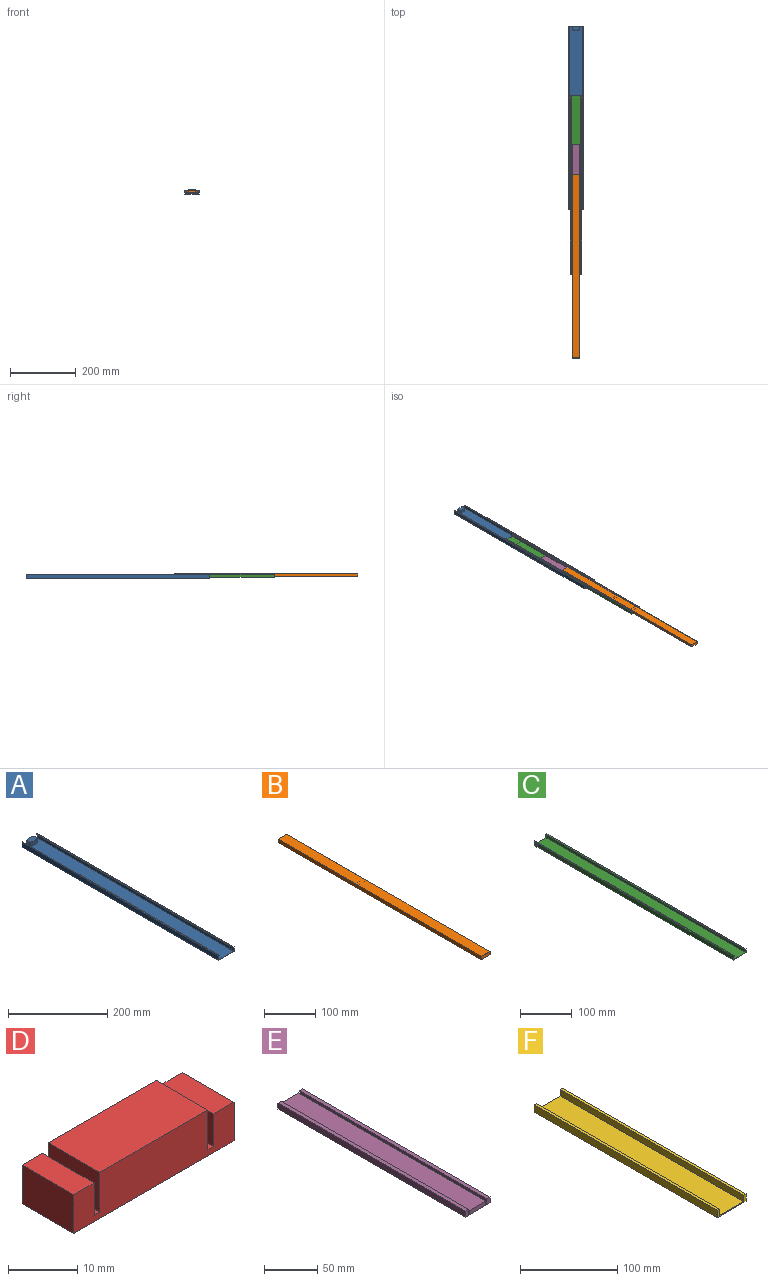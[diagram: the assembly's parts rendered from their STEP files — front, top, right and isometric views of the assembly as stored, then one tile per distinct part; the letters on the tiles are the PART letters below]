
ASSEMBLY  parts=6 mates=4
PART A: 30 faces, bbox 44.5x558.8x11.6 mm
  f0: plane 549.91x1.4mm, normal (0,0,-1), area 768.2mm2, adj f7,f8,f16,f28
  f1: plane 9.14x4.57mm, normal (-1,0,0), area 41.8mm2, adj f2,f5,f14,f29
  f2: plane 558.8x42.16mm, normal (0,0,1), area 23290.7mm2, adj f1,f4,f5,f6,f7,f8,f16,f17
  f3: plane 4.57x1.4mm, normal (0,0,-1), area 6.4mm2, adj f5,f6,f17,f27
  f4: plane 549.91x9.14mm, normal (1,0,0), area 5028.4mm2, adj f2,f7,f15,f26
  f5: plane 44.45x11.43mm, normal (0,-1,0), area 77.5mm2, adj f1,f2,f3,f6,f8,f9,f10,f11
  f6: plane 558.8x10.29mm, normal (1,0,0), area 678.2mm2, adj f2,f3,f5,f7,f10,f15,f26,f27
  f7: plane 44.45x11.56mm, normal (0,1,0), area 201.8mm2, adj f0,f2,f4,f6,f8,f9,f10,f11
  f8: plane 558.8x10.29mm, normal (-1,0,0), area 678.2mm2, adj f0,f2,f5,f7,f9,f14,f28,f29
  f9: plane 558.8x2.54mm, normal (0,0,1), area 1419.4mm2, adj f5,f7,f8,f11
  f10: plane 558.8x2.54mm, normal (0,0,1), area 1419.4mm2, adj f5,f6,f7,f12
  f11: plane 558.8x11.43mm, normal (1,0,0), area 6387.1mm2, adj f5,f7,f9,f13
  f12: plane 558.8x11.43mm, normal (-1,0,0), area 6387.1mm2, adj f5,f7,f10,f13
  f13: plane 558.8x44.45mm, normal (0,0,-1), area 24838.7mm2, adj f5,f7,f11,f12
  f14: plane 4.57x1.4mm, normal (0,0,-1), area 6.4mm2, adj f1,f5,f8,f29
  f15: plane 549.91x1.4mm, normal (0,0,-1), area 768.2mm2, adj f4,f6,f7,f26
  f16: plane 549.91x9.14mm, normal (-1,0,0), area 5028.4mm2, adj f0,f2,f7,f28
  f17: plane 9.14x4.57mm, normal (1,0,0), area 41.8mm2, adj f2,f3,f5,f27
  f18: plane 22.1x12.7mm, normal (0,0,1), area 258.5mm2, adj f7,f19,f20,f21,f22,f23,f24,f25
  f19: plane 10.41x2.54mm, normal (-1,0,0), area 26.5mm2, adj f2,f18,f23,f24
  f20: plane 10.41x2.54mm, normal (1,0,0), area 26.5mm2, adj f2,f18,f22,f25
  f21: plane 11.94x10.41mm, normal (0,-1,0), area 124.3mm2, adj f2,f18,f24,f25
  f22: cylinder r=5.08mm len=10.41mm, axis (0,0,-1), area 83.1mm2, adj f2,f7,f18,f20
  f23: cylinder r=5.08mm len=10.41mm, axis (0,0,1), area 83.1mm2, adj f2,f7,f18,f19
  f24: cylinder r=5.08mm len=10.41mm, axis (0,0,1), area 83.1mm2, adj f2,f18,f19,f21
  f25: cylinder r=5.08mm len=10.41mm, axis (0,0,-1), area 83.1mm2, adj f2,f18,f20,f21
  f26: plane 9.14x1.4mm, normal (0,1,0), area 12.8mm2, adj f2,f4,f6,f15
  f27: plane 9.14x1.4mm, normal (0,-1,0), area 12.8mm2, adj f2,f3,f6,f17
  f28: plane 9.14x1.4mm, normal (0,1,0), area 12.8mm2, adj f0,f2,f8,f16
  f29: plane 9.14x1.4mm, normal (0,-1,0), area 12.8mm2, adj f1,f2,f8,f14
PART B: 14 faces, bbox 24.4x558.8x8.1 mm
  f0: plane 212.73x22.1mm, normal (0,0,-1), area 4700.8mm2, adj f1,f2,f6,f12
  f1: plane 557.66x6.99mm, normal (1,0,0), area 3884.8mm2, adj f0,f3,f5,f6,f10,f11,f12,f13
  f2: plane 557.66x6.99mm, normal (-1,0,0), area 3884.8mm2, adj f0,f3,f5,f6,f10,f11,f12,f13
  f3: plane 338.58x22.1mm, normal (0,0,-1), area 7482mm2, adj f1,f2,f10,f11
  f4: plane 24.38x8.13mm, normal (0,-1,0), area 198.2mm2, adj f5,f7,f8,f9
  f5: plane 558.8x24.38mm, normal (0,0,-1), area 1302.7mm2, adj f1,f2,f4,f6,f7,f9,f10
  f6: plane 24.38x8.13mm, normal (0,1,0), area 43.8mm2, adj f0,f1,f2,f5,f7,f8,f9
  f7: plane 558.8x8.13mm, normal (1,0,0), area 4541.9mm2, adj f4,f5,f6,f8
  f8: plane 558.8x24.38mm, normal (0,0,1), area 13625.8mm2, adj f4,f6,f7,f9
  f9: plane 558.8x8.13mm, normal (-1,0,0), area 4541.9mm2, adj f4,f5,f6,f8
  f10: plane 22.1x6.99mm, normal (0,1,0), area 154.4mm2, adj f1,f2,f3,f5
  f11: plane 22.1x1.65mm, normal (0,-1,0), area 36.5mm2, adj f1,f2,f3,f13
  f12: plane 22.1x1.65mm, normal (0,1,0), area 36.5mm2, adj f0,f1,f2,f13
  f13: plane 22.1x6.35mm, normal (0,0,-1), area 140.3mm2, adj f1,f2,f11,f12
PART C: 24 faces, bbox 37.3x546.1x9.1 mm
  f0: plane 9.14x4.57mm, normal (-1,0,0), area 41.8mm2, adj f12,f14,f15,f21
  f1: plane 537.21x9.14mm, normal (1,0,0), area 4912.2mm2, adj f9,f10,f12,f19
  f2: plane 544.96x6.86mm, normal (1,0,0), area 3737.3mm2, adj f6,f7,f9,f17
  f3: plane 544.96x1.4mm, normal (0,0,-1), area 761.3mm2, adj f4,f5,f9,f16
  f4: plane 546.1x8mm, normal (-1,0,0), area 632mm2, adj f3,f6,f9,f10,f15,f16
  f5: plane 544.96x6.86mm, normal (-1,0,0), area 3737.3mm2, adj f3,f6,f9,f16
  f6: plane 546.1x32.77mm, normal (0,0,1), area 17890.3mm2, adj f2,f4,f5,f8,f9,f15,f16,f17
  f7: plane 544.96x1.4mm, normal (0,0,-1), area 761.3mm2, adj f2,f8,f9,f17
  f8: plane 546.1x8mm, normal (1,0,0), area 632mm2, adj f6,f7,f9,f14,f15,f17
  f9: plane 35.05x9.14mm, normal (0,-1,0), area 61.5mm2, adj f1,f2,f3,f4,f5,f6,f7,f8
  f10: plane 546.1x3.68mm, normal (0,0,1), area 1392mm2, adj f1,f4,f9,f11,f15,f18,f19,f20
  f11: plane 9.14x4.57mm, normal (1,0,0), area 41.8mm2, adj f10,f12,f15,f18
  f12: plane 546.1x37.34mm, normal (0,0,-1), area 19151.8mm2, adj f0,f1,f9,f11,f13,f15,f18,f19
  f13: plane 537.21x9.14mm, normal (-1,0,0), area 4912.2mm2, adj f9,f12,f14,f22
  f14: plane 546.1x3.68mm, normal (0,0,1), area 1392mm2, adj f0,f8,f9,f13,f15,f21,f22,f23
  f15: plane 35.05x9.14mm, normal (0,1,0), area 80.7mm2, adj f0,f4,f6,f8,f10,f11,f12,f14
  f16: plane 6.86x1.4mm, normal (0,-1,0), area 9.6mm2, adj f3,f4,f5,f6
  f17: plane 6.86x1.4mm, normal (0,-1,0), area 9.6mm2, adj f2,f6,f7,f8
  f18: plane 9.14x1.14mm, normal (0,1,0), area 10.5mm2, adj f10,f11,f12,f20
  f19: plane 9.14x1.14mm, normal (0,-1,0), area 10.5mm2, adj f1,f10,f12,f20
  f20: plane 9.14x4.32mm, normal (1,0,0), area 39.5mm2, adj f10,f12,f18,f19
  f21: plane 9.14x1.14mm, normal (0,1,0), area 10.5mm2, adj f0,f12,f14,f23
  f22: plane 9.14x1.14mm, normal (0,-1,0), area 10.5mm2, adj f12,f13,f14,f23
  f23: plane 9.14x4.32mm, normal (-1,0,0), area 39.5mm2, adj f12,f14,f21,f22
PART D: 14 faces, bbox 32.8x10.5x8.1 mm
  f0: plane 10.54x5.72mm, normal (-1,0,0), area 60.2mm2, adj f1,f10,f11,f12
  f1: plane 10.54x1.14mm, normal (0,0,1), area 12mm2, adj f0,f2,f11,f12
  f2: plane 10.54x6.99mm, normal (1,0,0), area 73.6mm2, adj f1,f11,f12,f13
  f3: plane 10.54x6.99mm, normal (-1,0,0), area 73.6mm2, adj f4,f11,f12,f13
  f4: plane 10.54x1.14mm, normal (0,0,1), area 12mm2, adj f3,f5,f11,f12
  f5: plane 10.54x5.72mm, normal (1,0,0), area 60.2mm2, adj f4,f6,f11,f12
  f6: plane 10.54x4.19mm, normal (0,0,1), area 44.2mm2, adj f5,f7,f11,f12
  f7: plane 10.54x6.86mm, normal (-1,0,0), area 72.3mm2, adj f6,f8,f11,f12
  f8: plane 32.77x10.54mm, normal (0,0,-1), area 345.4mm2, adj f7,f9,f11,f12
  f9: plane 10.54x6.86mm, normal (1,0,0), area 72.3mm2, adj f8,f10,f11,f12
  f10: plane 10.54x4.19mm, normal (0,0,1), area 44.2mm2, adj f0,f9,f11,f12
  f11: plane 32.77x8.13mm, normal (0,1,0), area 239.7mm2, adj f0,f1,f2,f3,f4,f5,f6,f7
  f12: plane 32.77x8.13mm, normal (0,-1,0), area 239.7mm2, adj f0,f1,f2,f3,f4,f5,f6,f7
  f13: plane 22.1x10.54mm, normal (0,0,1), area 232.9mm2, adj f2,f3,f11,f12
PART E: 14 faces, bbox 32.8x247.7x6.9 mm
  f0: plane 247.65x3.68mm, normal (-1,0,0), area 912.1mm2, adj f1,f2,f9,f13
  f1: plane 32.77x6.86mm, normal (0,-1,0), area 166.7mm2, adj f0,f3,f4,f5,f6,f7,f8,f9
  f2: plane 32.77x6.86mm, normal (0,1,0), area 166.7mm2, adj f0,f3,f4,f5,f6,f7,f8,f9
  f3: plane 247.65x32.77mm, normal (0,0,-1), area 8114.5mm2, adj f1,f2,f4,f12
  f4: plane 247.65x6.86mm, normal (1,0,0), area 1698.4mm2, adj f1,f2,f3,f5
  f5: plane 247.65x4.19mm, normal (0,0,1), area 1037.9mm2, adj f1,f2,f4,f6
  f6: plane 247.65x5.72mm, normal (-1,0,0), area 1415.3mm2, adj f1,f2,f5,f7
  f7: plane 247.65x1.14mm, normal (0,0,1), area 283.1mm2, adj f1,f2,f6,f8
  f8: plane 247.65x3.68mm, normal (1,0,0), area 912.1mm2, adj f1,f2,f7,f13
  f9: plane 247.65x1.14mm, normal (0,0,1), area 283.1mm2, adj f0,f1,f2,f10
  f10: plane 247.65x5.72mm, normal (1,0,0), area 1415.3mm2, adj f1,f2,f9,f11
  f11: plane 247.65x4.19mm, normal (0,0,1), area 1037.9mm2, adj f1,f2,f10,f12
  f12: plane 247.65x6.86mm, normal (-1,0,0), area 1698.4mm2, adj f1,f2,f3,f11
  f13: plane 247.65x22.1mm, normal (0,0,1), area 5472.6mm2, adj f0,f1,f2,f8
PART F: 10 faces, bbox 42.2x266.7x9.1 mm
  f0: plane 266.7x42.16mm, normal (0,0,-1), area 11245.1mm2, adj f1,f7,f8,f9
  f1: plane 266.7x9.14mm, normal (1,0,0), area 2438.7mm2, adj f0,f2,f8,f9
  f2: plane 266.7x3.56mm, normal (0,0,1), area 948.4mm2, adj f1,f3,f8,f9
  f3: plane 266.7x8mm, normal (-1,0,0), area 2133.9mm2, adj f2,f4,f8,f9
  f4: plane 266.7x35.05mm, normal (0,0,1), area 9348.4mm2, adj f3,f5,f8,f9
  f5: plane 266.7x8mm, normal (1,0,0), area 2133.9mm2, adj f4,f6,f8,f9
  f6: plane 266.7x3.56mm, normal (0,0,1), area 948.4mm2, adj f5,f7,f8,f9
  f7: plane 266.7x9.14mm, normal (-1,0,0), area 2438.7mm2, adj f0,f6,f8,f9
  f8: plane 42.16x9.14mm, normal (0,-1,0), area 105.1mm2, adj f0,f1,f2,f3,f4,f5,f6,f7
  f9: plane 42.16x9.14mm, normal (0,1,0), area 105.1mm2, adj f0,f1,f2,f3,f4,f5,f6,f7
PLACE A at identity fixed
PLACE B t=(0,-454.76,0)mm
PLACE C t=(0,-198.88,0)mm
PLACE D t=(0,-198.88,0)mm
PLACE E t=(0,-205.28,0)mm
PLACE F t=(0,-102.75,0)mm
MATE planar D.f13 <-> B.f3  axis (0,0,1) through (0,-192.47,11.56)mm
MATE planar C.f12 <-> F.f4  axis (0,0,-1) through (0,74.31,2.29)mm
MATE planar C.f6 <-> E.f3  axis (0,0,1) through (0,74.12,3.43)mm
MATE planar F.f0 <-> A.f2  axis (0,0,-1) through (0,176.65,1.14)mm
